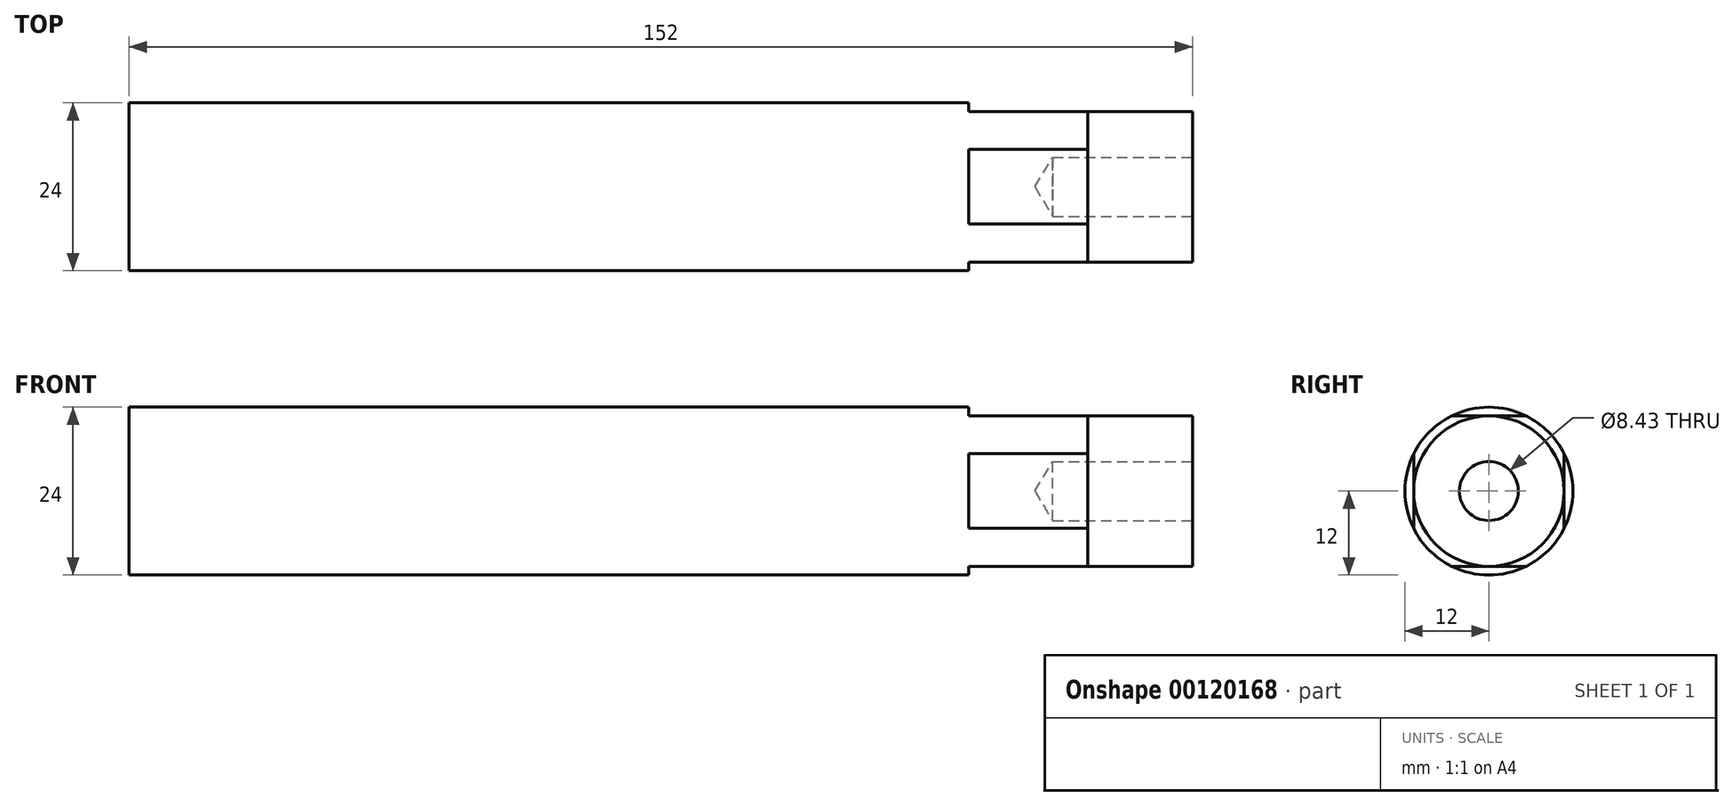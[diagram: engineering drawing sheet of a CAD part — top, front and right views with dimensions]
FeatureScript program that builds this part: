
annotation { "Feature Type Name" : "Feature", "Feature Type Description" : "" }
export const myFeature = defineFeature(function(context is Context, id is Id, definition is map)
    precondition{}
    {
        {
            var Q0;
            Q0=qCreatedBy(makeId("Right.planeOp"),FACE);
            var sketch = newSketch(context, id + "F0", { "sketchPlane" : qUnion([Q0])});
            skCircle(sketch, "E0", {"center": v(0, 0) * mm, "radius": 12 * mm});
            skSolve(sketch);
        }
        {
            var Q0;
            Q0=qSketchRegion(id+"F0",true);
            extrude(context, id + "F1", {"entities" : qUnion([Q0]), "endBound" : BoundingType.SYMMETRIC, "depth" : 152 * mm});
        }
        {
            var Q0;
            Q0=makeQuery(id+"F1.opExtrude","CAP_FACE",FACE,{"disambiguationData":[OSD([sQuery(id+"F0.wireOp",EDGE,"E0")])],"isStart":false});
            var sketch = newSketch(context, id + "F2", { "sketchPlane" : qUnion([Q0])});
            skLineSegment(sketch, "E1.bottom", {"start": v(-5.33, -10.75) * mm, "end": v(5.33, -10.75) * mm});
            skLineSegment(sketch, "E1.top", {"start": v(-5.33, 10.75) * mm, "end": v(5.33, 10.75) * mm});
            skLineSegment(sketch, "E1.left", {"start": v(-10.75, -5.33) * mm, "end": v(-10.75, 5.33) * mm});
            skLineSegment(sketch, "E1.right", {"start": v(10.75, -5.33) * mm, "end": v(10.75, 5.33) * mm});
            skPoint(sketch, "E1.middle", {"position": v(0, 0) * mm});
            skPoint(sketch, "E2.center.orphan", {"position": v(0, 12) * mm});
            skPoint(sketch, "E3.center.orphan", {"position": v(12, 0) * mm});
            skPoint(sketch, "E4.center.orphan", {"position": v(0, -12) * mm});
            skPoint(sketch, "E5.center.orphan", {"position": v(-12, 0) * mm});
            skArc(sketch, "E6.0", {"start": v(-10.75, 5.33) * mm, "mid": v(-12, 0) * mm, "end": v(-10.75, -5.33) * mm});
            skPoint(sketch, "E7.orphan", {"position": v(-10.75, 10.75) * mm});
            skPoint(sketch, "E8.orphan", {"position": v(10.75, 10.75) * mm});
            skPoint(sketch, "E9.orphan", {"position": v(10.75, -10.75) * mm});
            skPoint(sketch, "E10.orphan", {"position": v(-10.75, -10.75) * mm});
            skArc(sketch, "E11.trimOffspring", {"start": v(5.33, 10.75) * mm, "mid": v(0, 12) * mm, "end": v(-5.33, 10.75) * mm});
            skArc(sketch, "E12.trimOffspring", {"start": v(10.75, -5.33) * mm, "mid": v(12, 0) * mm, "end": v(10.75, 5.33) * mm});
            skArc(sketch, "E13.trimOffspring", {"start": v(-5.33, -10.75) * mm, "mid": v(0, -12) * mm, "end": v(5.33, -10.75) * mm});
            skSolve(sketch);
        }
        {
            var Q0;
            Q0=qSketchRegion(id+"F2",true);
            extrude(context, id + "F3", {"entities" : qUnion([Q0]), "operationType" : NewBodyOperationType.REMOVE, "oppositeDirection" : true, "depth" : 32 * mm});
        }
        {
            var Q0;
            Q0=makeQuery(id+"F1.opExtrude","CAP_FACE",FACE,{"disambiguationData":[OSD([sQuery(id+"F0.wireOp",EDGE,"E0")])],"isStart":false});
            var sketch = newSketch(context, id + "F4", { "sketchPlane" : qUnion([Q0])});
            skPoint(sketch, "E14", {"position": v(0, 0) * mm});
            skSolve(sketch);
        }
        {
            var Q0;
            Q0=sQuery(id+"F4.wireOp",VERTEX,"E14");
            var Q1;
            Q1=makeQuery(id+"F1.opExtrude","SWEPT_BODY",BODY,{"disambiguationData":[OSD([sQuery(id+"F0.wireOp",EDGE,"E0")])]});
            hole(context, id + "F5", {"style" : HoleStyle.SIMPLE, "endStyle" : HoleEndStyle.BLIND, "standardTappedOrClearance" : lookupTablePath({ "standard" : "ANSI", "engagement" : "75%", "pitch" : "24 tpi", "size" : "3/8", "type" : "Tapped" }), "standardBlindInLast" : lookupTablePath({ "standard" : "ANSI", "engagement" : "75%", "pitch" : "24 tpi", "size" : "3/8", "type" : "Tapped" }), "holeDiameter" : 8.43 * mm, "holeDepth" : 20 * mm, "startFromSketch" : true, "locations" : qUnion([Q0]), "scope" : qUnion([Q1]), "majorDiameter" : 9.53 * mm});
        }
        {
            var Q0;
            Q0=makeQuery(id+"F1.opExtrude","CAP_FACE",FACE,{"disambiguationData":[OSD([sQuery(id+"F0.wireOp",EDGE,"E0")])],"isStart":false});
            var sketch = newSketch(context, id + "F6", { "sketchPlane" : qUnion([Q0])});
            skCircle(sketch, "E15", {"center": v(0, 0) * mm, "radius": 10.75 * mm});
            skCircle(sketch, "E16", {"center": v(0, 0) * mm, "radius": 12 * mm});
            skSolve(sketch);
        }
        {
            var Q0;
            Q0 = qSketchRegion(id + "F6", true);
            extrude(context, id + "F7", {"entities" : qUnion([Q0]), "operationType" : NewBodyOperationType.REMOVE, "oppositeDirection" : true, "depth" : 15 * mm});
        }
    });
